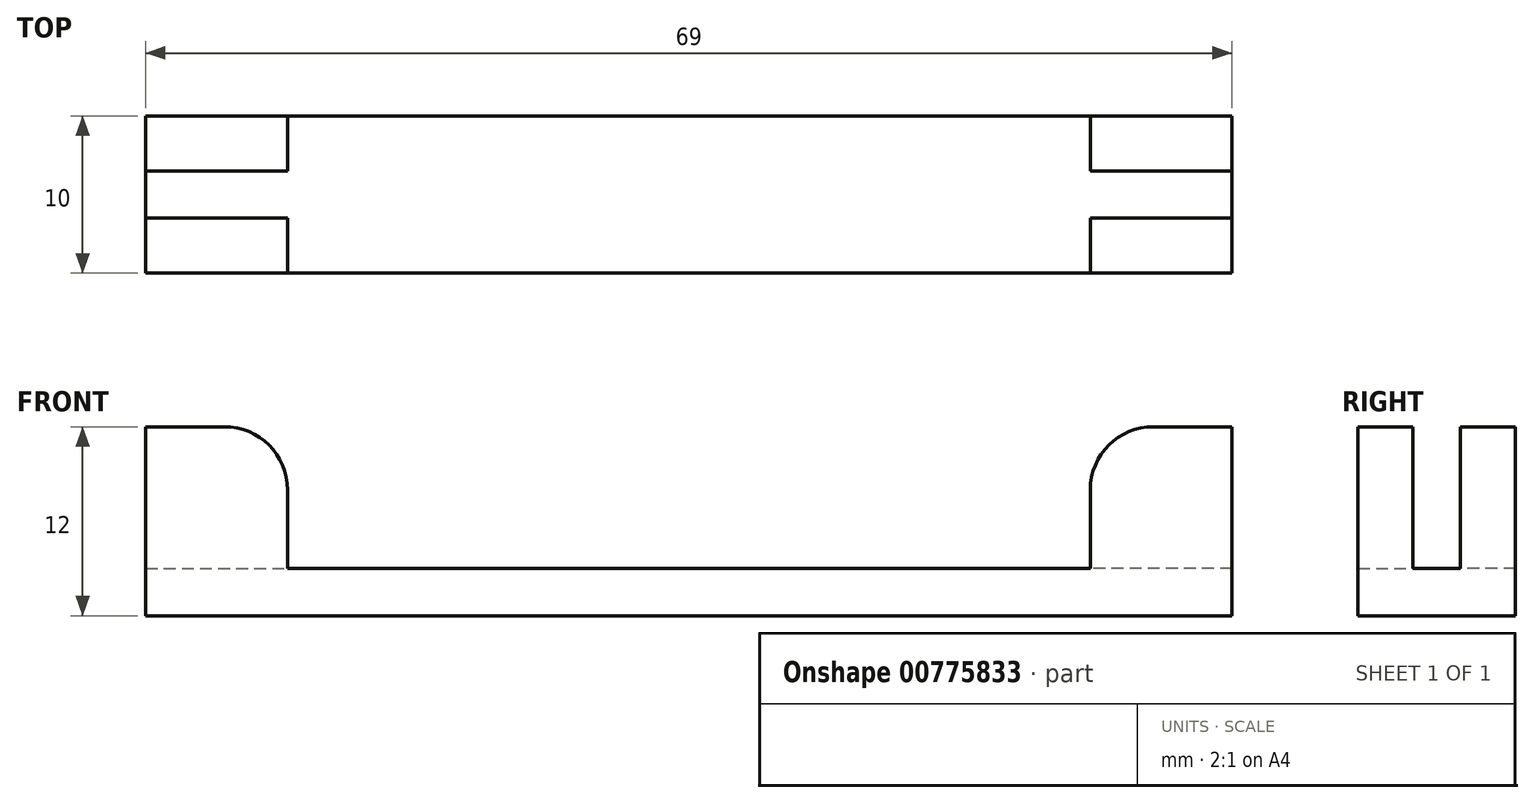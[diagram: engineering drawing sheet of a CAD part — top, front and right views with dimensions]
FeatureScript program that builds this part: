
annotation { "Feature Type Name" : "Feature", "Feature Type Description" : "" }
export const myFeature = defineFeature(function(context is Context, id is Id, definition is map)
    precondition{}
    {
        {
            assignVariable(context, id + "F0", {"name" : "speakerpostw", "anyValue" : 9 * mm});
        }
        {
            assignVariable(context, id + "F1", {"name" : "thick", "anyValue" : 3 * mm});
        }
        {
            var Q0;
            Q0=qCreatedBy(makeId("Top.planeOp"),FACE);
            var sketch = newSketch(context, id + "F2", { "sketchPlane" : qUnion([Q0])});
            skLineSegment(sketch, "E0.bottom", {"start": v(34.5, -5) * mm, "end": v(-34.5, -5) * mm});
            skLineSegment(sketch, "E0.top", {"start": v(34.5, 5) * mm, "end": v(-34.5, 5) * mm});
            skLineSegment(sketch, "E0.left", {"start": v(34.5, -5) * mm, "end": v(34.5, 5) * mm});
            skLineSegment(sketch, "E0.right", {"start": v(-34.5, -5) * mm, "end": v(-34.5, 5) * mm});
            skPoint(sketch, "E0.middle", {"position": v(0, 0) * mm});
            skSolve(sketch);
        }
        {
            var Q0;
            Q0=makeQuery(id+"F2.imprint","IMPRINT",FACE,{"disambiguationData":[TD([[makeQuery(id+"F2.imprint","IMPRINT",EDGE,{"derivedFrom":sQuery(id+"F2.wireOp",EDGE,"E0.bottom")}),-1.0]])]});
            extrude(context, id + "F3", {"entities" : qUnion([Q0]), "depth" : getVariable(context, 'thick'), "offsetDistance" : 25 * mm});
        }
        {
            var Q0;
            Q0=makeQuery(id+"F3.opExtrude","CAP_FACE",FACE,{"disambiguationData":[OSD([sQuery(id+"F2.wireOp",EDGE,"E0.bottom"),sQuery(id+"F2.wireOp",EDGE,"E0.top"),sQuery(id+"F2.wireOp",EDGE,"E0.left"),sQuery(id+"F2.wireOp",EDGE,"E0.right")])],"isStart":false});
            var sketch = newSketch(context, id + "F4", { "sketchPlane" : qUnion([Q0])});
            skLineSegment(sketch, "E1.bottom", {"start": v(-34.5, 5) * mm, "end": v(-25.5, 5) * mm});
            skLineSegment(sketch, "E1.top", {"start": v(-34.5, 1.5) * mm, "end": v(-25.5, 1.5) * mm});
            skLineSegment(sketch, "E1.left", {"start": v(-34.5, 5) * mm, "end": v(-34.5, 1.5) * mm});
            skLineSegment(sketch, "E1.right", {"start": v(-25.5, 5) * mm, "end": v(-25.5, 1.5) * mm});
            skSolve(sketch);
        }
        {
            var Q0;
            Q0=makeQuery(id+"F4.imprint","IMPRINT",FACE,{"disambiguationData":[TD([[makeQuery(id+"F4.imprint","IMPRINT",EDGE,{"derivedFrom":sQuery(id+"F4.wireOp",EDGE,"E1.bottom")}),1.0]])]});
            extrude(context, id + "F5", {"entities" : qUnion([Q0]), "operationType" : NewBodyOperationType.ADD, "depth" : getVariable(context, 'speakerpostw'), "offsetDistance" : 25 * mm});
        }
        {
            var Q0;
            Q0=makeQuery(id+"F5.opExtrude","CAP_EDGE",EDGE,{"disambiguationData":[OSD([sQuery(id+"F4.wireOp",EDGE,"E1.right")])],"isStart":false});
            fillet(context, id + "F6", {"entities" : qUnion([Q0]), "radius" : 4 * mm, "tangentPropagation" : true, "allowEdgeOverflow" : false});
        }
        {
            var Q0;
            Q0=makeQuery(id+"F3.opExtrude","SWEPT_BODY",BODY,{"disambiguationData":[OSD([sQuery(id+"F2.wireOp",EDGE,"E0.bottom"),sQuery(id+"F2.wireOp",EDGE,"E0.top"),sQuery(id+"F2.wireOp",EDGE,"E0.left"),sQuery(id+"F2.wireOp",EDGE,"E0.right")])]});
            var Q1;
            Q1=qCreatedBy(makeId("Right.planeOp"),FACE);
            mirror(context, id + "F7", {"operationType" : NewBodyOperationType.ADD, "entities" : qUnion([Q0]), "mirrorPlane" : qUnion([Q1])});
        }
        {
            var Q0;
            Q0=makeQuery(id+"F3.opExtrude","SWEPT_BODY",BODY,{"disambiguationData":[OSD([sQuery(id+"F2.wireOp",EDGE,"E0.bottom"),sQuery(id+"F2.wireOp",EDGE,"E0.top"),sQuery(id+"F2.wireOp",EDGE,"E0.left"),sQuery(id+"F2.wireOp",EDGE,"E0.right")])]});
            var Q1;
            Q1=qCreatedBy(makeId("Front.planeOp"),FACE);
            mirror(context, id + "F8", {"operationType" : NewBodyOperationType.ADD, "entities" : qUnion([Q0]), "mirrorPlane" : qUnion([Q1])});
        }
    });
